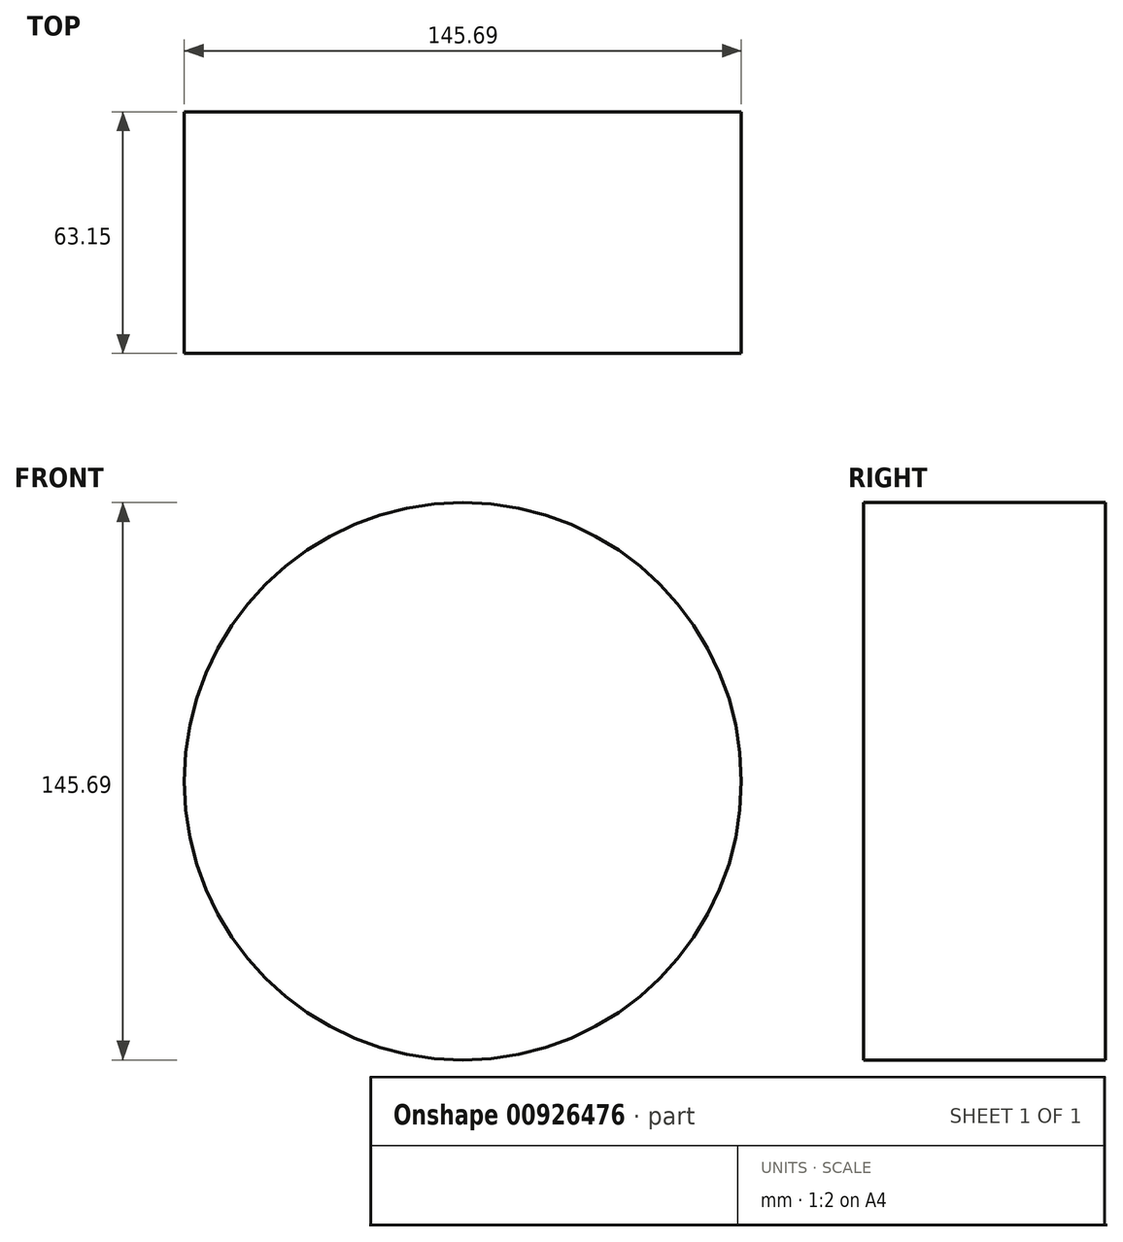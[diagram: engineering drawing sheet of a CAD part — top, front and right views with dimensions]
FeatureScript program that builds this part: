
annotation { "Feature Type Name" : "Feature", "Feature Type Description" : "" }
export const myFeature = defineFeature(function(context is Context, id is Id, definition is map)
    precondition{}
    {
        {
            var Q0;
            Q0=qCreatedBy(makeId("Front.planeOp"),FACE);
            var sketch = newSketch(context, id + "F0", { "sketchPlane" : qUnion([Q0])});
            skCircle(sketch, "E0", {"center": v(44.47, 57.7) * mm, "radius": 72.85 * mm});
            skSolve(sketch);
        }
        {
            var Q0;
            Q0=makeQuery(id+"F0.imprint","IMPRINT",FACE,{"disambiguationData":[TD([[makeQuery(id+"F0.imprint","IMPRINT",EDGE,{"derivedFrom":sQuery(id+"F0.wireOp",EDGE,"E0")}),1.0]])]});
            extrude(context, id + "F1", {"entities" : qUnion([Q0]), "depth" : 63.15 * mm, "offsetDistance" : 25.4 * mm});
        }
    });
